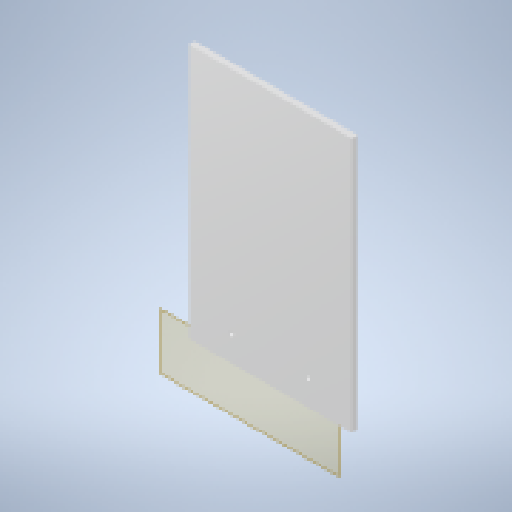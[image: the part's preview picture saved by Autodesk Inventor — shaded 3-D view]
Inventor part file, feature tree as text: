
AUTODESK INVENTOR PART (.ipt)
format: ipt  version: 2023.2 (Build 272271000, 271)  size: 254,464 bytes
history: native  units: mm
features: extrude x3, reference x3, other x3, sketch x2, projected_geometry x2, plane x1
ambient origin geometry x8: Origin, YZ Plane, XZ Plane, XY Plane, X Axis, Y Axis, Z Axis, Center Point
bodies: Solid1 (feature_tree)
feature tree (14):
  plane  "Work Plane1"
  extrude  "Extrusion1"  Depth=10.0mm TaperAngle=0.0deg
  extrude  "Extrusion2"  [1 undecoded]
  extrude  "Extrusion3"  [1 undecoded]
  reference  "Reference1"
  reference  "Reference2"
  reference  "Reference3"
  sketch  "Sketch2"  dims[d1=6.0mm d2=0.0mm d3=10.0mm d4=0.0mm]
  projected_geometry  "Projected Loop1"
  sketch  "Sketch3"  dims[d5=10.0mm d6=0.0mm]
  projected_geometry  "Projected Loop2"
  parser-record x1  (decoder bookkeeping rows leaked as tree rows — omitted from the tree; the rows remain in map.json)
  other  "Main Assembly.iam"
  other  "Joining Brace Front:1"
note: 2 required parameter values undecoded (feature->parameter linkage not recoverable at this tier; creation-order binding heuristic only, values carry confidence <= 0.55)
note: 1 file-system path scrubbed to <path> (originals preserved in map.json)
